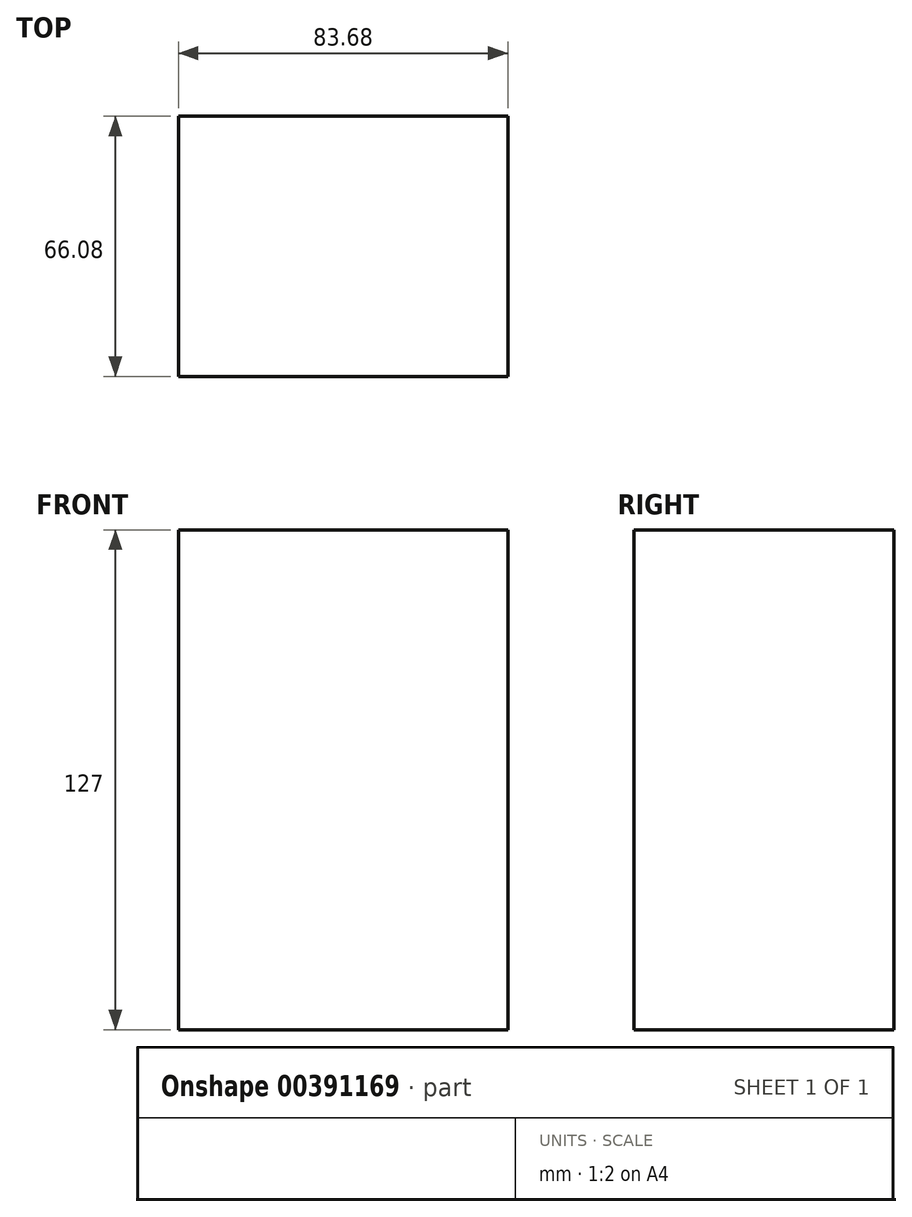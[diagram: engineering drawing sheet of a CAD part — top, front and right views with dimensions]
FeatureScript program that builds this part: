
annotation { "Feature Type Name" : "Feature", "Feature Type Description" : "" }
export const myFeature = defineFeature(function(context is Context, id is Id, definition is map)
    precondition{}
    {
        {
            var Q0;
            Q0=qCreatedBy(makeId("Top.planeOp"),FACE);
            var sketch = newSketch(context, id + "F0", { "sketchPlane" : qUnion([Q0])});
            skLineSegment(sketch, "E0.bottom", {"start": v(41.84, -33.04) * mm, "end": v(-41.84, -33.04) * mm});
            skLineSegment(sketch, "E0.top", {"start": v(41.84, 33.04) * mm, "end": v(-41.84, 33.04) * mm});
            skLineSegment(sketch, "E0.left", {"start": v(41.84, -33.04) * mm, "end": v(41.84, 33.04) * mm});
            skLineSegment(sketch, "E0.right", {"start": v(-41.84, -33.04) * mm, "end": v(-41.84, 33.04) * mm});
            skPoint(sketch, "E0.middle", {"position": v(0, 0) * mm});
            skSolve(sketch);
        }
        {
            var Q0;
            Q0 = qSketchRegion(id + "F0", true);
            extrude(context, id + "F1", {"entities" : qUnion([Q0]), "endBound" : BoundingType.SYMMETRIC, "depth" : 127 * mm});
        }
    });
